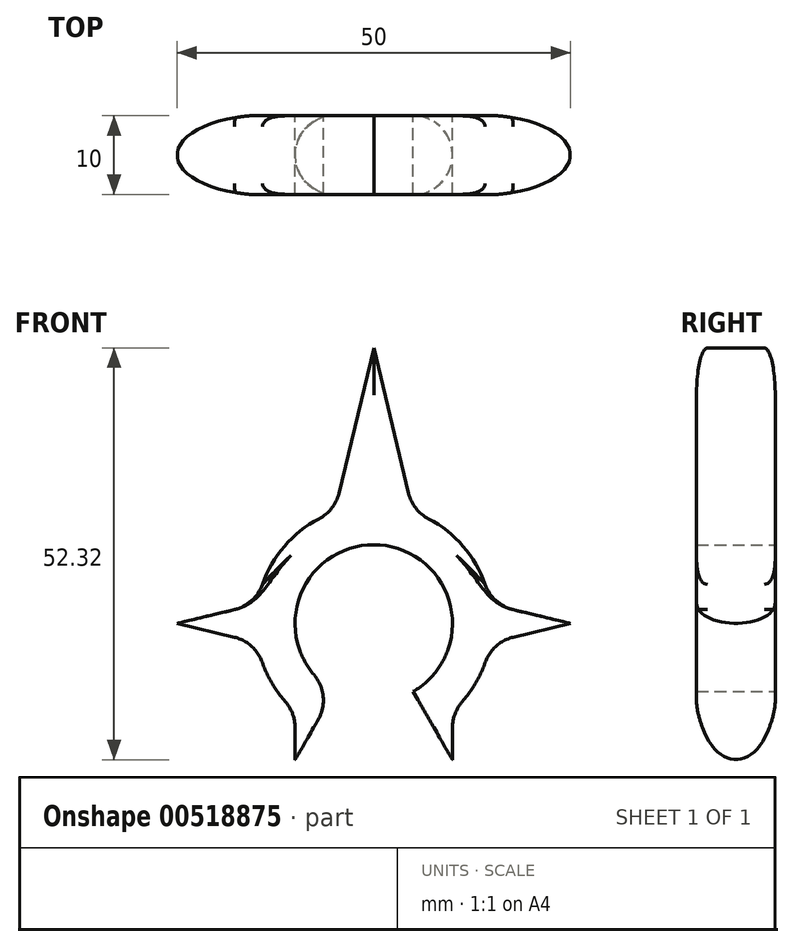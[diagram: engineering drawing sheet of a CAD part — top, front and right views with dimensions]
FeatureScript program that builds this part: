
annotation { "Feature Type Name" : "Feature", "Feature Type Description" : "" }
export const myFeature = defineFeature(function(context is Context, id is Id, definition is map)
    precondition{}
    {
        {
            var Q0;
            Q0=qCreatedBy(makeId("Front.planeOp"),FACE);
            var sketch = newSketch(context, id + "F0", { "sketchPlane" : qUnion([Q0])});
            skArc(sketch, "E0", {"start": v(5, -8.66) * mm, "mid": v(0, 10) * mm, "end": v(-5, -8.66) * mm});
            skArc(sketch, "E1", {"start": v(10, -11.18) * mm, "mid": v(0, 15) * mm, "end": v(-10, -11.18) * mm});
            skLineSegment(sketch, "E2", {"start": v(-5, -8.66) * mm, "end": v(-7.5, -13) * mm});
            skLineSegment(sketch, "E3", {"start": v(5, -8.66) * mm, "end": v(7.5, -13) * mm});
            skLineSegment(sketch, "E4", {"start": v(5, 14.14) * mm, "end": v(0, 35) * mm});
            skLineSegment(sketch, "E5", {"start": v(0, 35) * mm, "end": v(-5, 14.14) * mm});
            skLineSegment(sketch, "E6", {"start": v(-5, -8.66) * mm, "end": v(-10, -17.32) * mm});
            skLineSegment(sketch, "E7", {"start": v(-10, -17.32) * mm, "end": v(-10, -11.18) * mm});
            skLineSegment(sketch, "E8", {"start": v(5, -8.66) * mm, "end": v(10, -17.32) * mm});
            skLineSegment(sketch, "E9", {"start": v(10, -17.32) * mm, "end": v(10, -11.18) * mm});
            skPoint(sketch, "E10.trimOffspring.end.orphan", {"position": v(-8, 0) * mm});
            skPoint(sketch, "E11.trimOffspring.end.orphan", {"position": v(8, 0) * mm});
            skLineSegment(sketch, "E12", {"start": v(14.8, 2.45) * mm, "end": v(25, 0) * mm});
            skLineSegment(sketch, "E13", {"start": v(25, 0) * mm, "end": v(14.8, -2.45) * mm});
            skLineSegment(sketch, "E14", {"start": v(-14.8, 2.45) * mm, "end": v(-25, 0) * mm});
            skLineSegment(sketch, "E15", {"start": v(-25, 0) * mm, "end": v(-14.8, -2.45) * mm});
            skSolve(sketch);
        }
        {
            var Q0;
            Q0=qSketchRegion(id+"F0",true);
            extrude(context, id + "F1", {"entities" : qUnion([Q0]), "depth" : 10 * mm, "offsetDistance" : 25 * mm});
        }
        {
            var Q0;
            Q0=makeQuery(id+"F1.opExtrude","SWEPT_EDGE",EDGE,{"disambiguationData":[OSD([sQuery(id+"F0.wireOp",EDGE,"E1"),sQuery(id+"F0.wireOp",EDGE,"E5")])]});
            fillet(context, id + "F2", {"entities" : qUnion([Q0]), "radius" : 5 * mm, "tangentPropagation" : true, "allowEdgeOverflow" : false});
        }
        {
            var Q0;
            Q0=makeQuery(id+"F1.opExtrude","SWEPT_EDGE",EDGE,{"disambiguationData":[OSD([sQuery(id+"F0.wireOp",EDGE,"E1"),sQuery(id+"F0.wireOp",EDGE,"E4")])]});
            fillet(context, id + "F3", {"entities" : qUnion([Q0]), "radius" : 5 * mm, "tangentPropagation" : true, "allowEdgeOverflow" : false});
        }
        {
            var Q0;
            Q0=makeQuery(id+"F1.opExtrude","SWEPT_EDGE",EDGE,{"disambiguationData":[OSD([sQuery(id+"F0.wireOp",EDGE,"E0"),sQuery(id+"F0.wireOp",EDGE,"E2")])]});
            fillet(context, id + "F4", {"entities" : qUnion([Q0]), "radius" : 5 * mm, "tangentPropagation" : true, "allowEdgeOverflow" : false});
        }
        {
            var Q0;
            Q0=makeQuery(id+"F1.opExtrude","SWEPT_EDGE",EDGE,{"disambiguationData":[OSD([sQuery(id+"F0.wireOp",EDGE,"E1"),sQuery(id+"F0.wireOp",EDGE,"E7")])]});
            fillet(context, id + "F5", {"entities" : qUnion([Q0]), "radius" : 5 * mm, "tangentPropagation" : true, "allowEdgeOverflow" : false});
        }
        {
            var Q0;
            Q0=makeQuery(id+"F1.opExtrude","SWEPT_EDGE",EDGE,{"disambiguationData":[OSD([sQuery(id+"F0.wireOp",EDGE,"E1"),sQuery(id+"F0.wireOp",EDGE,"E9")])]});
            fillet(context, id + "F6", {"entities" : qUnion([Q0]), "radius" : 5 * mm, "tangentPropagation" : true, "allowEdgeOverflow" : false});
        }
        {
            var Q0;
            Q0=makeQuery(id+"F1.opExtrude","CAP_EDGE",EDGE,{"disambiguationData":[OSD([sQuery(id+"F0.wireOp",EDGE,"E4")])],"isStart":false});
            var Q1;
            Q1=makeQuery(id+"F1.opExtrude","CAP_EDGE",EDGE,{"disambiguationData":[OSD([sQuery(id+"F0.wireOp",EDGE,"E5")])],"isStart":false});
            fillet(context, id + "F7", {"entities" : qUnion([Q0, Q1]), "radius" : 1.4 * mm, "tangentPropagation" : true, "allowEdgeOverflow" : false});
        }
        {
            var Q0;
            Q0=makeQuery(id+"F1.opExtrude","CAP_EDGE",EDGE,{"disambiguationData":[OSD([sQuery(id+"F0.wireOp",EDGE,"E4")])],"isStart":true});
            var Q1;
            Q1=makeQuery(id+"F1.opExtrude","CAP_EDGE",EDGE,{"disambiguationData":[OSD([sQuery(id+"F0.wireOp",EDGE,"E5")])],"isStart":true});
            fillet(context, id + "F8", {"entities" : qUnion([Q0, Q1]), "radius" : 1.4 * mm, "tangentPropagation" : true, "allowEdgeOverflow" : false});
        }
        {
            var Q0;
            Q0=makeQuery(id+"F1.opExtrude","SWEPT_EDGE",EDGE,{"disambiguationData":[OSD([sQuery(id+"F0.wireOp",EDGE,"E1"),sQuery(id+"F0.wireOp",EDGE,"E14")])]});
            var Q1;
            Q1=makeQuery(id+"F1.opExtrude","SWEPT_EDGE",EDGE,{"disambiguationData":[OSD([sQuery(id+"F0.wireOp",EDGE,"E1"),sQuery(id+"F0.wireOp",EDGE,"E12")])]});
            var Q2;
            Q2=makeQuery(id+"F1.opExtrude","SWEPT_EDGE",EDGE,{"disambiguationData":[OSD([sQuery(id+"F0.wireOp",EDGE,"E1"),sQuery(id+"F0.wireOp",EDGE,"E13")])]});
            var Q3;
            Q3=makeQuery(id+"F1.opExtrude","SWEPT_EDGE",EDGE,{"disambiguationData":[OSD([sQuery(id+"F0.wireOp",EDGE,"E1"),sQuery(id+"F0.wireOp",EDGE,"E15")])]});
            fillet(context, id + "F9", {"entities" : qUnion([Q0, Q1, Q2, Q3]), "radius" : 5 * mm, "tangentPropagation" : true, "allowEdgeOverflow" : false});
        }
        {
            var Q0;
            {var subQ0=sQuery(id+"F0.wireOp",EDGE,"E1");Q0=makeQuery(id+"F1.opExtrude","CAP_EDGE",EDGE,{"disambiguationData":[OSD([subQ0]),TDD([makeQuery(id+"F0.imprint","IMPRINT",EDGE,{"disambiguationData":[TD([[makeQuery(id+"F0.imprint","INTERSECT",VERTEX,{"derivedFrom":[subQ0,sQuery(id+"F0.wireOp",EDGE,"E9")]}),-1.0]])],"derivedFrom":subQ0})])],"isStart":true});}
            var Q1;
            {var subQ0=sQuery(id+"F0.wireOp",EDGE,"E1");Q1=makeQuery(id+"F1.opExtrude","CAP_EDGE",EDGE,{"disambiguationData":[OSD([subQ0]),TDD([makeQuery(id+"F0.imprint","IMPRINT",EDGE,{"disambiguationData":[TD([[makeQuery(id+"F0.imprint","INTERSECT",VERTEX,{"derivedFrom":[subQ0,sQuery(id+"F0.wireOp",EDGE,"E9")]}),-1.0]])],"derivedFrom":subQ0})])],"isStart":false});}
            fillet(context, id + "F10", {"entities" : qUnion([Q0, Q1]), "radius" : 5 * mm, "tangentPropagation" : true, "allowEdgeOverflow" : false});
        }
        {
            var Q0;
            {var subQ0=sQuery(id+"F0.wireOp",EDGE,"E1");Q0=makeQuery(id+"F1.opExtrude","CAP_EDGE",EDGE,{"disambiguationData":[OSD([subQ0]),TDD([makeQuery(id+"F0.imprint","IMPRINT",EDGE,{"disambiguationData":[TD([[makeQuery(id+"F0.imprint","INTERSECT",VERTEX,{"derivedFrom":[subQ0,sQuery(id+"F0.wireOp",EDGE,"E7")]}),1.0]])],"derivedFrom":subQ0})])],"isStart":false});}
            var Q1;
            {var subQ0=sQuery(id+"F0.wireOp",EDGE,"E1");Q1=makeQuery(id+"F1.opExtrude","CAP_EDGE",EDGE,{"disambiguationData":[OSD([subQ0]),TDD([makeQuery(id+"F0.imprint","IMPRINT",EDGE,{"disambiguationData":[TD([[makeQuery(id+"F0.imprint","INTERSECT",VERTEX,{"derivedFrom":[subQ0,sQuery(id+"F0.wireOp",EDGE,"E7")]}),1.0]])],"derivedFrom":subQ0})])],"isStart":true});}
            fillet(context, id + "F11", {"entities" : qUnion([Q0, Q1]), "radius" : 5 * mm, "tangentPropagation" : true, "allowEdgeOverflow" : false});
        }
    });
